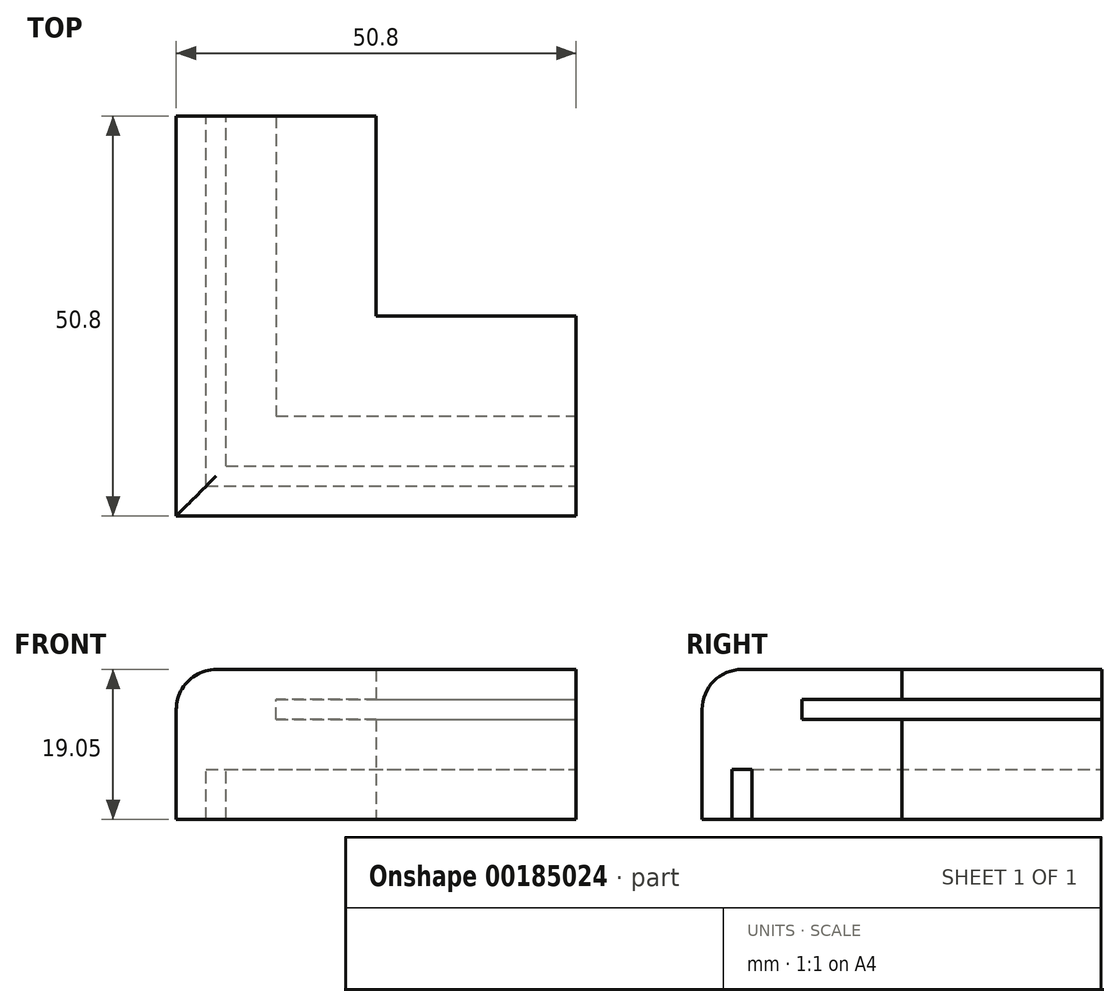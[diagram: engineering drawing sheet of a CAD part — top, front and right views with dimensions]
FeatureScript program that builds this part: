
annotation { "Feature Type Name" : "Feature", "Feature Type Description" : "" }
export const myFeature = defineFeature(function(context is Context, id is Id, definition is map)
    precondition{}
    {
        {
            var Q0;
            Q0=qCreatedBy(makeId("Top.planeOp"),FACE);
            var sketch = newSketch(context, id + "F0", { "sketchPlane" : qUnion([Q0])});
            skLineSegment(sketch, "E0.bottom", {"start": v(0, 0) * mm, "end": v(50.8, 0) * mm});
            skLineSegment(sketch, "E0.top", {"start": v(25.4, 25.4) * mm, "end": v(50.8, 25.4) * mm});
            skLineSegment(sketch, "E0.left", {"start": v(0, 0) * mm, "end": v(0, 25.4) * mm});
            skLineSegment(sketch, "E0.right", {"start": v(50.8, 0) * mm, "end": v(50.8, 25.4) * mm});
            skLineSegment(sketch, "E1.bottom", {"start": v(0, 0) * mm, "end": v(25.4, 0) * mm});
            skLineSegment(sketch, "E1.top", {"start": v(0, 50.8) * mm, "end": v(25.4, 50.8) * mm});
            skLineSegment(sketch, "E1.left", {"start": v(0, 0) * mm, "end": v(0, 50.8) * mm});
            skLineSegment(sketch, "E1.right", {"start": v(25.4, 25.4) * mm, "end": v(25.4, 50.8) * mm});
            skSolve(sketch);
        }
        {
            var Q0;
            Q0=makeQuery(id+"F0.imprint","IMPRINT",FACE,{"disambiguationData":[TD([[makeQuery(id+"F0.imprint","IMPRINT",EDGE,{"derivedFrom":sQuery(id+"F0.wireOp",EDGE,"E0.bottom")}),1.0]])]});
            extrude(context, id + "F1", {"entities" : qUnion([Q0]), "depth" : 19.05 * mm});
        }
        {
            var Q0;
            Q0=makeQuery(id+"F1.opExtrude","SWEPT_FACE",FACE,{"disambiguationData":[OSD([sQuery(id+"F0.wireOp",EDGE,"E0.right")])]});
            var sketch = newSketch(context, id + "F2", { "sketchPlane" : qUnion([Q0])});
            skLineSegment(sketch, "E2.bottom", {"start": v(3.81, 0) * mm, "end": v(6.35, 0) * mm});
            skLineSegment(sketch, "E2.top", {"start": v(3.8, 6.35) * mm, "end": v(6.35, 6.35) * mm});
            skLineSegment(sketch, "E2.left", {"start": v(3.81, 0) * mm, "end": v(3.8, 6.35) * mm});
            skLineSegment(sketch, "E2.right", {"start": v(6.35, 0) * mm, "end": v(6.35, 6.35) * mm});
            skLineSegment(sketch, "E3.bottom", {"start": v(25.4, 12.7) * mm, "end": v(12.7, 12.7) * mm});
            skLineSegment(sketch, "E3.top", {"start": v(25.4, 15.24) * mm, "end": v(12.7, 15.24) * mm});
            skLineSegment(sketch, "E3.left", {"start": v(25.4, 12.7) * mm, "end": v(25.4, 15.24) * mm});
            skLineSegment(sketch, "E3.right", {"start": v(12.7, 12.7) * mm, "end": v(12.7, 15.24) * mm});
            skSolve(sketch);
        }
        {
            var Q0;
            Q0=makeQuery(id+"F2.imprint","IMPRINT",FACE,{"disambiguationData":[TD([[makeQuery(id+"F2.imprint","IMPRINT",EDGE,{"derivedFrom":sQuery(id+"F2.wireOp",EDGE,"E2.bottom")}),1.0]])]});
            extrude(context, id + "F3", {"entities" : qUnion([Q0]), "operationType" : NewBodyOperationType.REMOVE, "oppositeDirection" : true, "depth" : 47 * mm});
        }
        {
            var Q0;
            Q0=makeQuery(id+"F2.imprint","IMPRINT",FACE,{"disambiguationData":[TD([[makeQuery(id+"F2.imprint","IMPRINT",EDGE,{"derivedFrom":sQuery(id+"F2.wireOp",EDGE,"E3.bottom")}),-1.0]])]});
            extrude(context, id + "F4", {"entities" : qUnion([Q0]), "operationType" : NewBodyOperationType.REMOVE, "oppositeDirection" : true, "depth" : 38.1 * mm});
        }
        {
            var Q0;
            Q0=makeQuery(id+"F1.opExtrude","SWEPT_FACE",FACE,{"disambiguationData":[OSD([sQuery(id+"F0.wireOp",EDGE,"E1.top")])]});
            var sketch = newSketch(context, id + "F5", { "sketchPlane" : qUnion([Q0])});
            skLineSegment(sketch, "E4.bottom", {"start": v(-25.4, 12.7) * mm, "end": v(-12.7, 12.7) * mm});
            skLineSegment(sketch, "E4.top", {"start": v(-25.4, 15.24) * mm, "end": v(-12.7, 15.24) * mm});
            skLineSegment(sketch, "E4.left", {"start": v(-25.4, 12.7) * mm, "end": v(-25.4, 15.24) * mm});
            skLineSegment(sketch, "E4.right", {"start": v(-12.7, 12.7) * mm, "end": v(-12.7, 15.24) * mm});
            skLineSegment(sketch, "E5.bottom", {"start": v(-3.8, 0) * mm, "end": v(-6.35, 0) * mm});
            skLineSegment(sketch, "E5.top", {"start": v(-3.81, 6.35) * mm, "end": v(-6.35, 6.35) * mm});
            skLineSegment(sketch, "E5.left", {"start": v(-3.8, 0) * mm, "end": v(-3.81, 6.35) * mm});
            skLineSegment(sketch, "E5.right", {"start": v(-6.35, 0) * mm, "end": v(-6.35, 6.35) * mm});
            skSolve(sketch);
        }
        {
            var Q0;
            Q0=makeQuery(id+"F5.imprint","IMPRINT",FACE,{"disambiguationData":[TD([[makeQuery(id+"F5.imprint","IMPRINT",EDGE,{"derivedFrom":sQuery(id+"F5.wireOp",EDGE,"E4.bottom")}),1.0]])]});
            extrude(context, id + "F6", {"entities" : qUnion([Q0]), "operationType" : NewBodyOperationType.REMOVE, "oppositeDirection" : true, "depth" : 38.1 * mm});
        }
        {
            var Q0;
            Q0=makeQuery(id+"F5.imprint","IMPRINT",FACE,{"disambiguationData":[TD([[makeQuery(id+"F5.imprint","IMPRINT",EDGE,{"derivedFrom":sQuery(id+"F5.wireOp",EDGE,"E5.bottom")}),-1.0]])]});
            extrude(context, id + "F7", {"entities" : qUnion([Q0]), "operationType" : NewBodyOperationType.REMOVE, "oppositeDirection" : true, "depth" : 46.74 * mm});
        }
        {
            var Q0;
            Q0=makeQuery(id+"F1.opExtrude","CAP_EDGE",EDGE,{"disambiguationData":[OSD([sQuery(id+"F0.wireOp",EDGE,"E0.bottom"),sQuery(id+"F0.wireOp",EDGE,"E1.bottom")])],"isStart":false});
            var Q1;
            Q1=makeQuery(id+"F1.opExtrude","CAP_EDGE",EDGE,{"disambiguationData":[OSD([sQuery(id+"F0.wireOp",EDGE,"E1.left")])],"isStart":false});
            fillet(context, id + "F8", {"entities" : qUnion([Q0, Q1]), "radius" : 5.08 * mm, "tangentPropagation" : true, "allowEdgeOverflow" : false});
        }
    });
